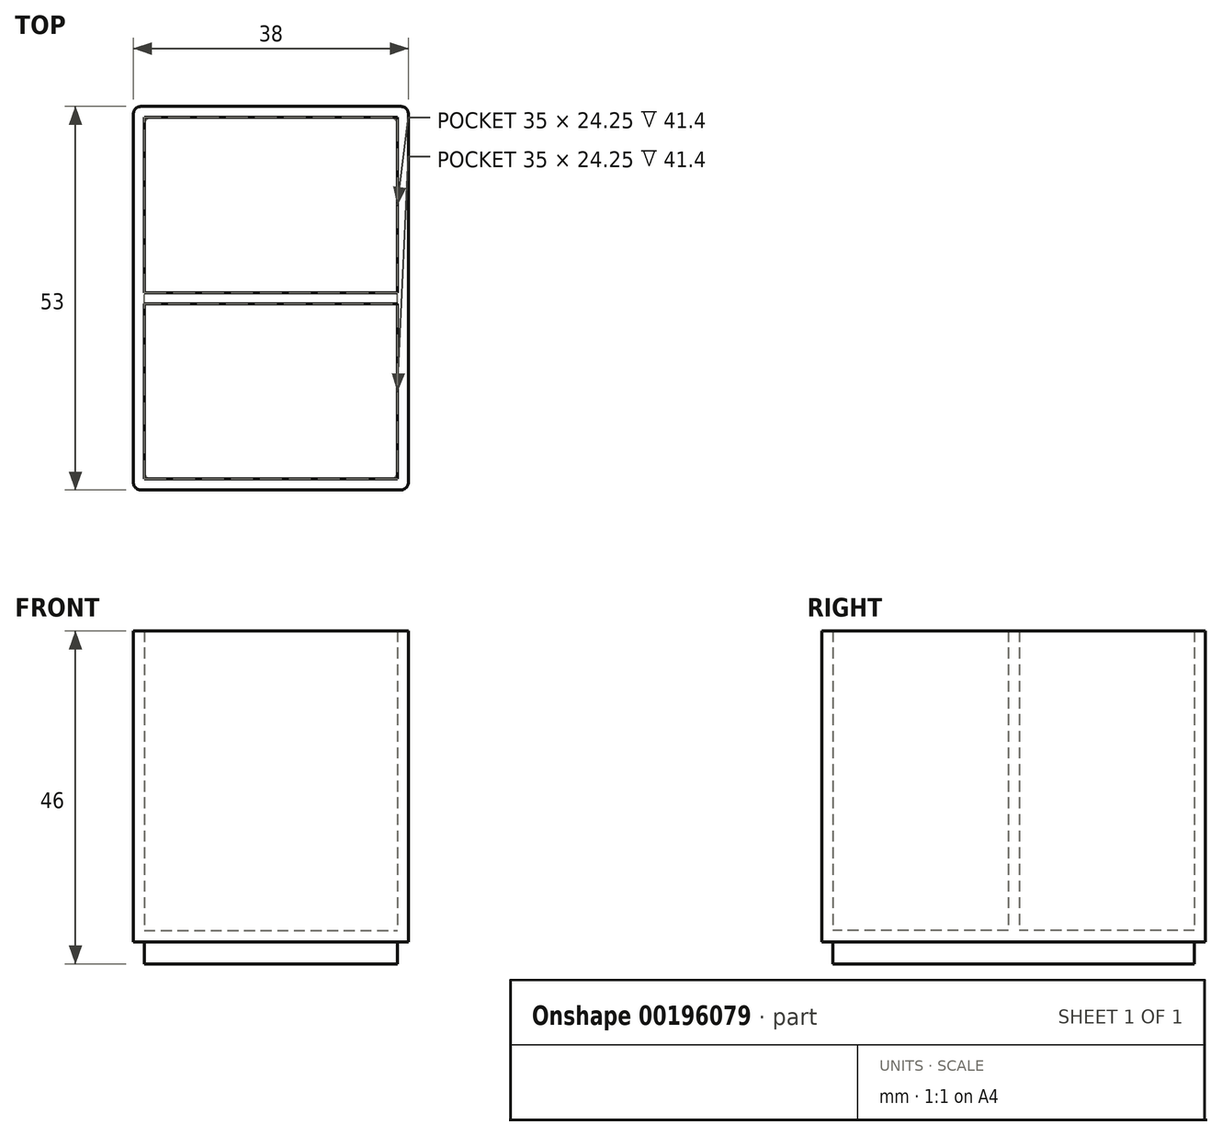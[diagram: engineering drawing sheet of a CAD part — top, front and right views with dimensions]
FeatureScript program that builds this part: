
annotation { "Feature Type Name" : "Feature", "Feature Type Description" : "" }
export const myFeature = defineFeature(function(context is Context, id is Id, definition is map)
    precondition{}
    {
        {
            var Q0;
            Q0=qCreatedBy(makeId("Top.planeOp"),FACE);
            var sketch = newSketch(context, id + "F0", { "sketchPlane" : qUnion([Q0])});
            skLineSegment(sketch, "E0.bottom", {"start": v(0, 0) * mm, "end": v(38, 0) * mm});
            skLineSegment(sketch, "E0.top", {"start": v(0, 53) * mm, "end": v(38, 53) * mm});
            skLineSegment(sketch, "E0.left", {"start": v(0, 0) * mm, "end": v(0, 53) * mm});
            skLineSegment(sketch, "E0.right", {"start": v(38, 0) * mm, "end": v(38, 53) * mm});
            skLineSegment(sketch, "E1.bottom", {"start": v(1.5, 1.5) * mm, "end": v(36.5, 1.5) * mm});
            skLineSegment(sketch, "E1.top", {"start": v(1.5, 51.5) * mm, "end": v(36.5, 51.5) * mm});
            skLineSegment(sketch, "E1.left", {"start": v(1.5, 1.5) * mm, "end": v(1.5, 51.5) * mm});
            skLineSegment(sketch, "E1.right", {"start": v(36.5, 1.5) * mm, "end": v(36.5, 51.5) * mm});
            skSolve(sketch);
        }
        {
            var Q0;
            Q0=makeQuery(id+"F0.imprint","IMPRINT",FACE,{"disambiguationData":[TD([[makeQuery(id+"F0.imprint","IMPRINT",EDGE,{"derivedFrom":sQuery(id+"F0.wireOp",EDGE,"E1.bottom")}),1.0]])]});
            extrude(context, id + "F1", {"entities" : qUnion([Q0]), "oppositeDirection" : true, "depth" : 3 * mm, "offsetDistance" : 25 * mm});
        }
        {
            var Q0;
            Q0=makeQuery(id+"F0.imprint","IMPRINT",FACE,{"disambiguationData":[TD([[makeQuery(id+"F0.imprint","IMPRINT",EDGE,{"derivedFrom":sQuery(id+"F0.wireOp",EDGE,"E0.bottom")}),1.0]])]});
            var Q1;
            Q1=makeQuery(id+"F0.imprint","IMPRINT",FACE,{"disambiguationData":[TD([[makeQuery(id+"F0.imprint","IMPRINT",EDGE,{"derivedFrom":sQuery(id+"F0.wireOp",EDGE,"E1.bottom")}),1.0]])]});
            extrude(context, id + "F2", {"entities" : qUnion([Q0, Q1]), "operationType" : NewBodyOperationType.ADD, "depth" : 1.6 * mm, "offsetDistance" : 25 * mm});
        }
        {
            var Q0;
            Q0=makeQuery(id+"F0.imprint","IMPRINT",FACE,{"disambiguationData":[TD([[makeQuery(id+"F0.imprint","IMPRINT",EDGE,{"derivedFrom":sQuery(id+"F0.wireOp",EDGE,"E0.bottom")}),1.0]])]});
            extrude(context, id + "F3", {"entities" : qUnion([Q0]), "operationType" : NewBodyOperationType.ADD, "depth" : 43 * mm, "offsetDistance" : 25 * mm});
        }
        {
            var Q0;
            Q0=makeQuery(id+"F1.opExtrude","SWEPT_EDGE",EDGE,{"disambiguationData":[OSD([sQuery(id+"F0.wireOp",EDGE,"E1.bottom"),sQuery(id+"F0.wireOp",EDGE,"E1.right")])]});
            var Q1;
            Q1=makeQuery(id+"F1.opExtrude","SWEPT_EDGE",EDGE,{"disambiguationData":[OSD([sQuery(id+"F0.wireOp",EDGE,"E1.bottom"),sQuery(id+"F0.wireOp",EDGE,"E1.left")])]});
            var Q2;
            Q2=makeQuery(id+"F1.opExtrude","SWEPT_EDGE",EDGE,{"disambiguationData":[OSD([sQuery(id+"F0.wireOp",EDGE,"E1.top"),sQuery(id+"F0.wireOp",EDGE,"E1.left")])]});
            var Q3;
            Q3=makeQuery(id+"F1.opExtrude","SWEPT_EDGE",EDGE,{"disambiguationData":[OSD([sQuery(id+"F0.wireOp",EDGE,"E1.top"),sQuery(id+"F0.wireOp",EDGE,"E1.right")])]});
            var Q4;
            {var subQ0=sQuery(id+"F0.wireOp",EDGE,"E0.left");var subQ1=sQuery(id+"F0.wireOp",EDGE,"E0.top");Q4=makeQuery(id+"F3.boolean.opBoolean","MERGE",EDGE,{"derivedFrom":[makeQuery(id+"F2.opExtrude","SWEPT_EDGE",EDGE,{"disambiguationData":[OSD([subQ1,subQ0])]}),makeQuery(id+"F3.opExtrude","SWEPT_EDGE",EDGE,{"disambiguationData":[OSD([subQ1,subQ0])]})]});}
            var Q5;
            {var subQ0=sQuery(id+"F0.wireOp",EDGE,"E0.right");var subQ1=sQuery(id+"F0.wireOp",EDGE,"E0.top");Q5=makeQuery(id+"F3.boolean.opBoolean","MERGE",EDGE,{"derivedFrom":[makeQuery(id+"F2.opExtrude","SWEPT_EDGE",EDGE,{"disambiguationData":[OSD([subQ1,subQ0])]}),makeQuery(id+"F3.opExtrude","SWEPT_EDGE",EDGE,{"disambiguationData":[OSD([subQ1,subQ0])]})]});}
            var Q6;
            {var subQ0=sQuery(id+"F0.wireOp",EDGE,"E0.left");var subQ1=sQuery(id+"F0.wireOp",EDGE,"E0.bottom");Q6=makeQuery(id+"F3.boolean.opBoolean","MERGE",EDGE,{"derivedFrom":[makeQuery(id+"F2.opExtrude","SWEPT_EDGE",EDGE,{"disambiguationData":[OSD([subQ1,subQ0])]}),makeQuery(id+"F3.opExtrude","SWEPT_EDGE",EDGE,{"disambiguationData":[OSD([subQ1,subQ0])]})]});}
            var Q7;
            {var subQ0=sQuery(id+"F0.wireOp",EDGE,"E0.right");var subQ1=sQuery(id+"F0.wireOp",EDGE,"E0.bottom");Q7=makeQuery(id+"F3.boolean.opBoolean","MERGE",EDGE,{"derivedFrom":[makeQuery(id+"F2.opExtrude","SWEPT_EDGE",EDGE,{"disambiguationData":[OSD([subQ1,subQ0])]}),makeQuery(id+"F3.opExtrude","SWEPT_EDGE",EDGE,{"disambiguationData":[OSD([subQ1,subQ0])]})]});}
            fillet(context, id + "F4", {"entities" : qUnion([Q0, Q1, Q2, Q3, Q4, Q5, Q6, Q7]), "radius" : 1 * mm, "tangentPropagation" : true, "allowEdgeOverflow" : false});
        }
        {
            var Q0;
            Q0=makeQuery(id+"F2.opExtrude","CAP_FACE",FACE,{"disambiguationData":[OSD([sQuery(id+"F0.wireOp",EDGE,"E0.bottom"),sQuery(id+"F0.wireOp",EDGE,"E0.top"),sQuery(id+"F0.wireOp",EDGE,"E0.left"),sQuery(id+"F0.wireOp",EDGE,"E0.right")])],"isStart":false});
            var sketch = newSketch(context, id + "F5", { "sketchPlane" : qUnion([Q0])});
            skLineSegment(sketch, "E2", {"start": v(1.5, 26.5) * mm, "end": v(36.5, 26.5) * mm, "construction": true});
            skLineSegment(sketch, "E3", {"start": v(1.5, 25.75) * mm, "end": v(36.5, 25.75) * mm});
            skLineSegment(sketch, "E4.MirrorCS", {"start": v(1.5, 27.25) * mm, "end": v(36.5, 27.25) * mm});
            skSolve(sketch);
        }
        {
            var Q0;
            {var subQ0=sQuery(id+"F5.wireOp",EDGE,"E3");Q0=makeQuery(id+"F5.imprint","IMPRINT",FACE,{"disambiguationData":[TD([[makeQuery(id+"F5.imprint","IMPRINT",EDGE,{"derivedFrom":subQ0}),1.0]])]});}
            var Q1;
            Q1=makeQuery(id+"F3.opExtrude","CAP_FACE",FACE,{"disambiguationData":[OSD([sQuery(id+"F0.wireOp",EDGE,"E0.bottom"),sQuery(id+"F0.wireOp",EDGE,"E0.top"),sQuery(id+"F0.wireOp",EDGE,"E0.left"),sQuery(id+"F0.wireOp",EDGE,"E0.right"),sQuery(id+"F0.wireOp",EDGE,"E1.bottom"),sQuery(id+"F0.wireOp",EDGE,"E1.top"),sQuery(id+"F0.wireOp",EDGE,"E1.left"),sQuery(id+"F0.wireOp",EDGE,"E1.right")])],"isStart":false});
            extrude(context, id + "F6", {"entities" : qUnion([Q0]), "operationType" : NewBodyOperationType.ADD, "endBound" : BoundingType.UP_TO_SURFACE, "depth" : 25 * mm, "endBoundEntityFace" : qUnion([Q1]), "offsetDistance" : 25 * mm});
        }
    });
